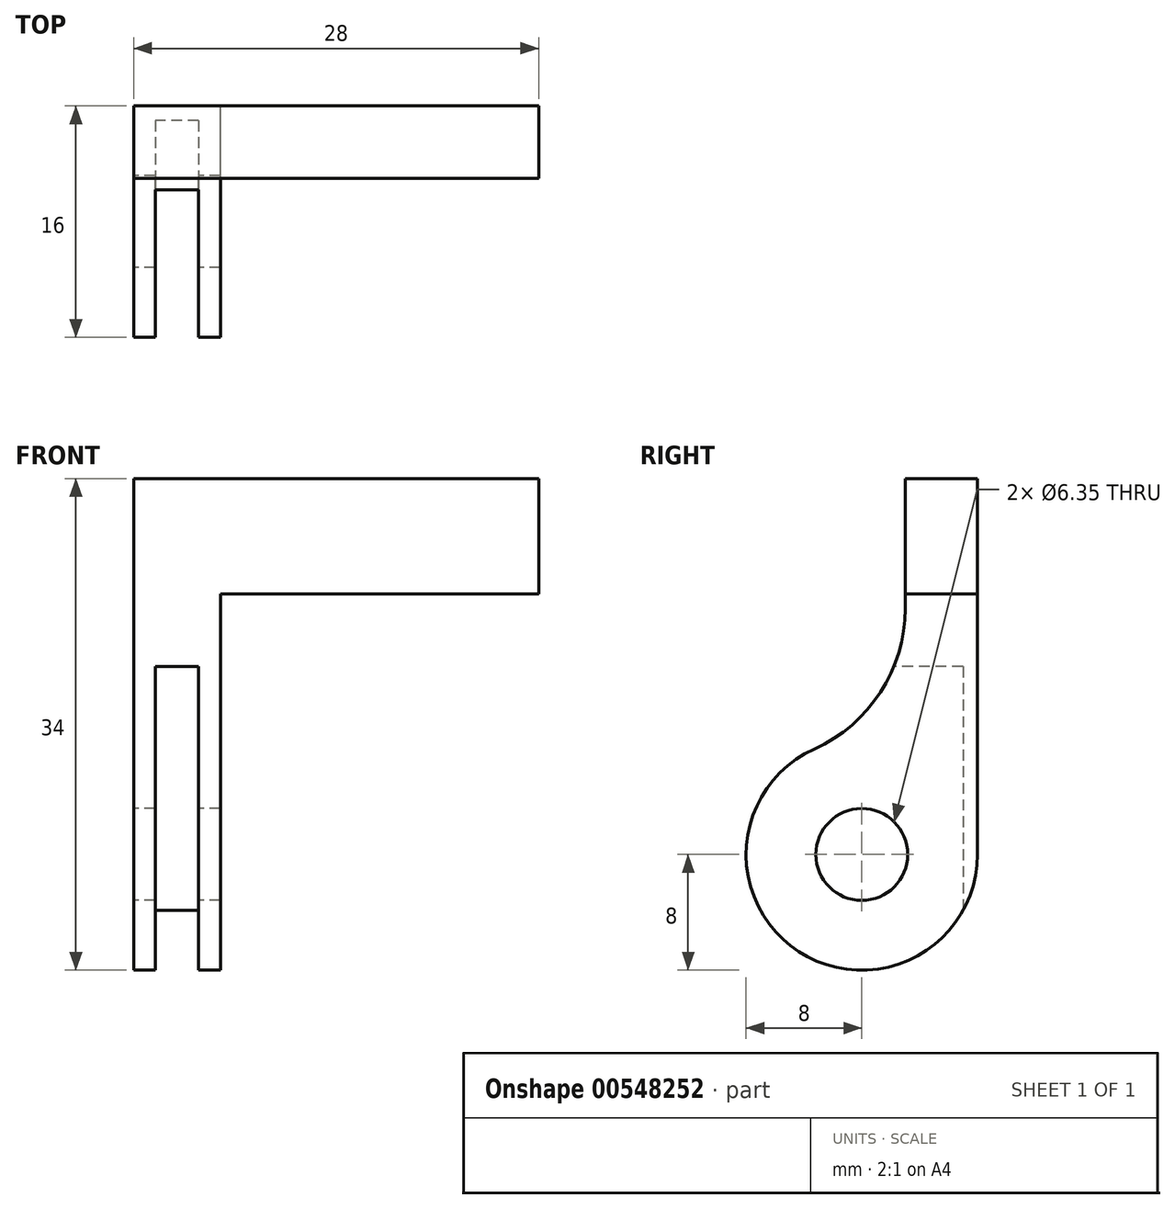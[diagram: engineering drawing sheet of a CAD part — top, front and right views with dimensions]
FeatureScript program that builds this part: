
annotation { "Feature Type Name" : "Feature", "Feature Type Description" : "" }
export const myFeature = defineFeature(function(context is Context, id is Id, definition is map)
    precondition{}
    {
        {
            var Q0;
            Q0=qCreatedBy(makeId("Right.planeOp"),FACE);
            cPlane(context, id + "F0", {"entities" : qUnion([Q0]), "cplaneType" : CPlaneType.OFFSET, "offset" : 28 * mm, "oppositeDirection" : true, "width" : 150 * mm, "height" : 150 * mm});
        }
        {
            var Q0;
            Q0=qCreatedBy(id+"F0.planeOp",FACE);
            var sketch = newSketch(context, id + "F1", { "sketchPlane" : qUnion([Q0])});
            skLineSegment(sketch, "E0", {"start": v(2.5, 4) * mm, "end": v(-2.5, 4) * mm});
            skLineSegment(sketch, "E1", {"start": v(-2.5, 4) * mm, "end": v(-2.5, -5) * mm});
            skLineSegment(sketch, "E2", {"start": v(2.5, 4) * mm, "end": v(2.5, -22) * mm});
            skArc(sketch, "E3", {"start": v(-8.78, -14.7) * mm, "mid": v(-9.85, -28.72) * mm, "end": v(2.5, -22) * mm});
            skLineSegment(sketch, "E4", {"start": v(0, 4) * mm, "end": v(0, 0) * mm, "construction": true});
            skArc(sketch, "E5", {"start": v(-8.78, -14.7) * mm, "mid": v(-4.2, -10.78) * mm, "end": v(-2.5, -5) * mm});
            skSolve(sketch);
        }
        {
            var Q0;
            Q0=makeQuery(id+"F1.imprint","IMPRINT",FACE,{"disambiguationData":[TD([[makeQuery(id+"F1.imprint","IMPRINT",EDGE,{"derivedFrom":sQuery(id+"F1.wireOp",EDGE,"E0")}),1.0]])]});
            extrude(context, id + "F2", {"entities" : qUnion([Q0]), "depth" : 6 * mm, "offsetDistance" : 25 * mm});
        }
        {
            var Q0;
            Q0=makeQuery(id+"F2.opExtrude","CAP_FACE",FACE,{"disambiguationData":[OSD([sQuery(id+"F1.wireOp",EDGE,"E0"),sQuery(id+"F1.wireOp",EDGE,"E1"),sQuery(id+"F1.wireOp",EDGE,"E2"),sQuery(id+"F1.wireOp",EDGE,"E3"),sQuery(id+"F1.wireOp",EDGE,"E5")])],"isStart":true});
            var sketch = newSketch(context, id + "F3", { "sketchPlane" : qUnion([Q0])});
            skPoint(sketch, "E6", {"position": v(5.5, -22) * mm});
            skSolve(sketch);
        }
        {
            var Q0;
            Q0=sQuery(id+"F3.wireOp",VERTEX,"E6");
            var Q1;
            Q1=makeQuery(id+"F2.opExtrude","SWEPT_BODY",BODY,{"disambiguationData":[OSD([sQuery(id+"F1.wireOp",EDGE,"E0"),sQuery(id+"F1.wireOp",EDGE,"E1"),sQuery(id+"F1.wireOp",EDGE,"E2"),sQuery(id+"F1.wireOp",EDGE,"E3"),sQuery(id+"F1.wireOp",EDGE,"E5")])]});
            hole(context, id + "F4", {"style" : HoleStyle.SIMPLE, "endStyle" : HoleEndStyle.THROUGH, "holeDiameter" : 6.35 * mm, "isTappedThrough" : true, "tappedDepth" : 12 * mm, "tapClearance" : 3, "locations" : qUnion([Q0]), "scope" : qUnion([Q1])});
        }
        {
            var Q0;
            Q0=makeQuery(id+"F2.opExtrude","CAP_FACE",FACE,{"disambiguationData":[OSD([sQuery(id+"F1.wireOp",EDGE,"E0"),sQuery(id+"F1.wireOp",EDGE,"E1"),sQuery(id+"F1.wireOp",EDGE,"E2"),sQuery(id+"F1.wireOp",EDGE,"E3"),sQuery(id+"F1.wireOp",EDGE,"E5")])],"isStart":false});
            var sketch = newSketch(context, id + "F5", { "sketchPlane" : qUnion([Q0])});
            skLineSegment(sketch, "E7.bottom", {"start": v(-2.5, 4) * mm, "end": v(2.5, 4) * mm});
            skLineSegment(sketch, "E7.top", {"start": v(-2.5, -4) * mm, "end": v(2.5, -4) * mm});
            skLineSegment(sketch, "E7.left", {"start": v(-2.5, 4) * mm, "end": v(-2.5, -4) * mm});
            skLineSegment(sketch, "E7.right", {"start": v(2.5, 4) * mm, "end": v(2.5, -4) * mm});
            skSolve(sketch);
        }
        {
            var Q0;
            Q0=qCreatedBy(makeId("Front.planeOp"),FACE);
            cPlane(context, id + "F6", {"entities" : qUnion([Q0]), "cplaneType" : CPlaneType.OFFSET, "offset" : 13.5 * mm, "width" : 150 * mm, "height" : 150 * mm});
        }
        {
            var Q0;
            Q0=qCreatedBy(id+"F6.planeOp",FACE);
            var sketch = newSketch(context, id + "F7", { "sketchPlane" : qUnion([Q0])});
            skLineSegment(sketch, "E8.bottom", {"start": v(-26.5, -9) * mm, "end": v(-23.5, -9) * mm});
            skLineSegment(sketch, "E8.top", {"start": v(-26.5, -35.89) * mm, "end": v(-23.5, -35.89) * mm});
            skLineSegment(sketch, "E8.left", {"start": v(-26.5, -9) * mm, "end": v(-26.5, -35.89) * mm});
            skLineSegment(sketch, "E8.right", {"start": v(-23.5, -9) * mm, "end": v(-23.5, -35.89) * mm});
            skLineSegment(sketch, "E9.0", {"start": v(-22, 4) * mm, "end": v(-28, 4) * mm});
            skLineSegment(sketch, "E10.0", {"start": v(-22, -14.7) * mm, "end": v(-22, -30) * mm});
            skLineSegment(sketch, "E10.1", {"start": v(-28, -14.7) * mm, "end": v(-28, -30) * mm});
            skSolve(sketch);
        }
        {
            var Q0;
            Q0=makeQuery(id+"F7.imprint","IMPRINT",FACE,{"disambiguationData":[TD([[makeQuery(id+"F7.imprint","IMPRINT",EDGE,{"derivedFrom":sQuery(id+"F7.wireOp",EDGE,"E8.bottom")}),-1.0]])]});
            extrude(context, id + "F8", {"entities" : qUnion([Q0]), "operationType" : NewBodyOperationType.REMOVE, "oppositeDirection" : true, "depth" : 15 * mm, "offsetDistance" : 25 * mm});
        }
        {
            var Q0;
            Q0=makeQuery(id+"F5.imprint","IMPRINT",FACE,{"disambiguationData":[TD([[makeQuery(id+"F5.imprint","IMPRINT",EDGE,{"derivedFrom":sQuery(id+"F5.wireOp",EDGE,"E7.bottom")}),1.0]])]});
            var Q1;
            Q1=qCreatedBy(makeId("Right.planeOp"),FACE);
            extrude(context, id + "F9", {"entities" : qUnion([Q0]), "operationType" : NewBodyOperationType.ADD, "endBound" : BoundingType.UP_TO_SURFACE, "depth" : 25 * mm, "endBoundEntityFace" : qUnion([Q1]), "offsetDistance" : 25 * mm});
        }
    });
